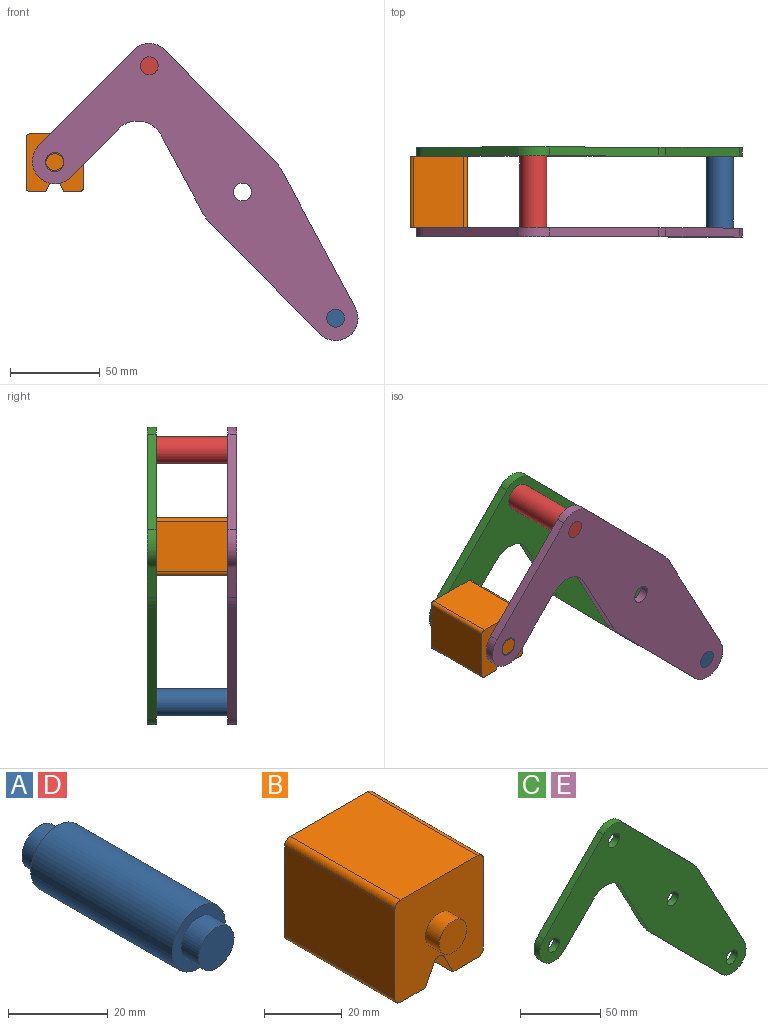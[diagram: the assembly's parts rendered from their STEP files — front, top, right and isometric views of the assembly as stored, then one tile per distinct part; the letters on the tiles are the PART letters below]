
ASSEMBLY  parts=5 mates=3
PART A: 7 faces, bbox 15x50x15 mm
  f0: cylinder r=7.5mm len=40mm, axis (0,-1,0), area 1885mm2, adj f2,f5
  f1: cylinder r=5mm len=10mm, axis (0,1,0), area 157.1mm2, adj f2,f3
  f2: plane 15x15mm, normal (0,-1,0), area 98.2mm2, adj f0,f1
  f3: plane 10x10mm, normal (0,-1,0), area 78.5mm2, adj f1
  f4: cylinder r=5mm len=10mm, axis (0,-1,0), area 157.1mm2, adj f5,f6
  f5: plane 15x15mm, normal (0,1,0), area 98.2mm2, adj f0,f4
  f6: plane 10x10mm, normal (0,1,0), area 78.5mm2, adj f4
PART B: 18 faces, bbox 32.1x50x32.1 mm
  f0: plane 40x28.08mm, normal (1,0,0), area 1123.1mm2, adj f4,f10,f13,f14
  f1: plane 40x9.04mm, normal (0,0,-1), area 361.6mm2, adj f2,f4,f10,f14
  f2: plane 40x6.42mm, normal (-0.89,0,-0.45), area 287.2mm2, adj f1,f4,f10,f15
  f3: plane 40x6.42mm, normal (0.89,0,-0.45), area 287.2mm2, adj f4,f5,f10,f15
  f4: plane 32.08x32.08mm, normal (0,-1,0), area 900.6mm2, adj f0,f1,f2,f3,f5,f6,f7,f9
  f5: plane 40x9.04mm, normal (0,0,-1), area 361.6mm2, adj f3,f4,f10,f16
  f6: plane 40x28.08mm, normal (0,0,1), area 1123.1mm2, adj f4,f10,f13,f17
  f7: plane 40x28.08mm, normal (-1,0,0), area 1123.1mm2, adj f4,f10,f16,f17
  f8: plane 10x10mm, normal (0,-1,0), area 78.5mm2, adj f9
  f9: cylinder r=5mm len=10mm, axis (0,1,0), area 157.1mm2, adj f4,f8
  f10: plane 32.08x32.08mm, normal (0,1,0), area 900.6mm2, adj f0,f1,f2,f3,f5,f6,f7,f12
  f11: plane 10x10mm, normal (0,1,0), area 78.5mm2, adj f12
  f12: cylinder r=5mm len=10mm, axis (0,-1,0), area 157.1mm2, adj f10,f11
  f13: cylinder r=2mm len=40mm, axis (0,1,0), area 125.7mm2, adj f0,f4,f6,f10
  f14: cylinder r=2mm len=40mm, axis (0,-1,0), area 125.7mm2, adj f0,f1,f4,f10
  f15: cylinder r=2mm len=40mm, axis (0,1,0), area 177.1mm2, adj f2,f3,f4,f10
  f16: cylinder r=2mm len=40mm, axis (0,1,0), area 125.7mm2, adj f4,f5,f7,f10
  f17: cylinder r=2mm len=40mm, axis (0,-1,0), area 125.7mm2, adj f4,f6,f7,f10
PART C: 18 faces, bbox 181.7x5x165.8 mm
  f0: plane 43.49x23.35mm, normal (-0.88,0,-0.47), area 246.8mm2, adj f1,f14,f16,f17
  f1: cylinder r=25mm len=5.75mm, axis (0,1,0), area 35.8mm2, adj f0,f2,f16,f17
  f2: plane 61.6x60.87mm, normal (-0.71,0,-0.7), area 433mm2, adj f1,f3,f16,f17
  f3: cylinder r=12.5mm len=21.39mm, axis (0,1,0), area 178.4mm2, adj f2,f4,f16,f17
  f4: plane 76.3x40.96mm, normal (0.88,0,0.47), area 433mm2, adj f3,f5,f16,f17
  f5: cylinder r=25mm len=5.75mm, axis (0,1,0), area 35.8mm2, adj f4,f6,f16,f17
  f6: plane 61.6x60.87mm, normal (0.71,0,0.7), area 433mm2, adj f5,f7,f16,f17
  f7: cylinder r=12.5mm len=17.78mm, axis (0,1,0), area 98.9mm2, adj f6,f8,f16,f17
  f8: plane 53.35x52.71mm, normal (-0.71,0,0.7), area 375mm2, adj f7,f9,f16,f17
  f9: cylinder r=12.5mm len=21.39mm, axis (0,1,0), area 196.3mm2, adj f8,f10,f16,f17
  f10: plane 26.86x26.54mm, normal (0.71,0,-0.7), area 188.8mm2, adj f9,f14,f16,f17
  f11: cylinder r=5mm len=10mm, axis (0,1,0), area 157.1mm2, adj f16,f17
  f12: cylinder r=5mm len=10mm, axis (0,1,0), area 157.1mm2, adj f16,f17
  f13: cylinder r=5mm len=10mm, axis (0,1,0), area 157.1mm2, adj f16,f17
  f14: cylinder r=15mm len=23.89mm, axis (0,1,0), area 140.2mm2, adj f0,f10,f16,f17
  f15: cylinder r=5mm len=10mm, axis (0,1,0), area 157.1mm2, adj f16,f17
  f16: plane 181.66x165.78mm, normal (0,-1,0), area 8710.1mm2, adj f0,f1,f2,f3,f4,f5,f6,f7
  f17: plane 181.66x165.78mm, normal (0,1,0), area 8710.1mm2, adj f0,f1,f2,f3,f4,f5,f6,f7
PART D: same geometry as A
PART E: same geometry as C
PLACE A t=(103.95,-20,-140.78)mm
PLACE B t=(0,-20,-0.67)mm
PLACE C t=(0,25,0)mm
PLACE D t=(0,-20,0)mm
PLACE E t=(0,-20,0)mm fixed
MATE fastened C.f7 <-> D.f0  axis (0,-1,0) through (-51.98,20,70.39)mm
MATE revolute E.f9 <-> B.f4  axis (0,1,0) through (-104.69,-20,17.04)mm
MATE fastened A.f0 <-> E.f3  axis (0,-1,0) through (51.98,-20,-70.39)mm
